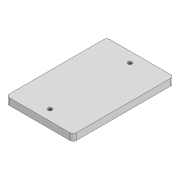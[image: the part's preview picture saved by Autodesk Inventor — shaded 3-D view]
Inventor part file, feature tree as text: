
AUTODESK INVENTOR PART (.ipt)
format: ipt  version: 2020 (Build 240168000, 168)  size: 91,136 bytes
history: native  units: mm
features: extrude x1, fillet x1, sketch x1
ambient origin geometry x8: Origin, YZ Plane, XZ Plane, XY Plane, X Axis, Y Axis, Z Axis, Center Point
bodies: Solid1 (feature_tree)
feature tree (3):
  extrude  "Extrusion1"  Depth=100.0mm
  fillet  "Fillet1"  Radius=59.5mm
  sketch  "Sketch1"  dims[d0=150.0mm d1=100.0mm d2=59.5mm d3=5.6mm d4=10.0mm d5=0.0mm d6=5.0mm]
